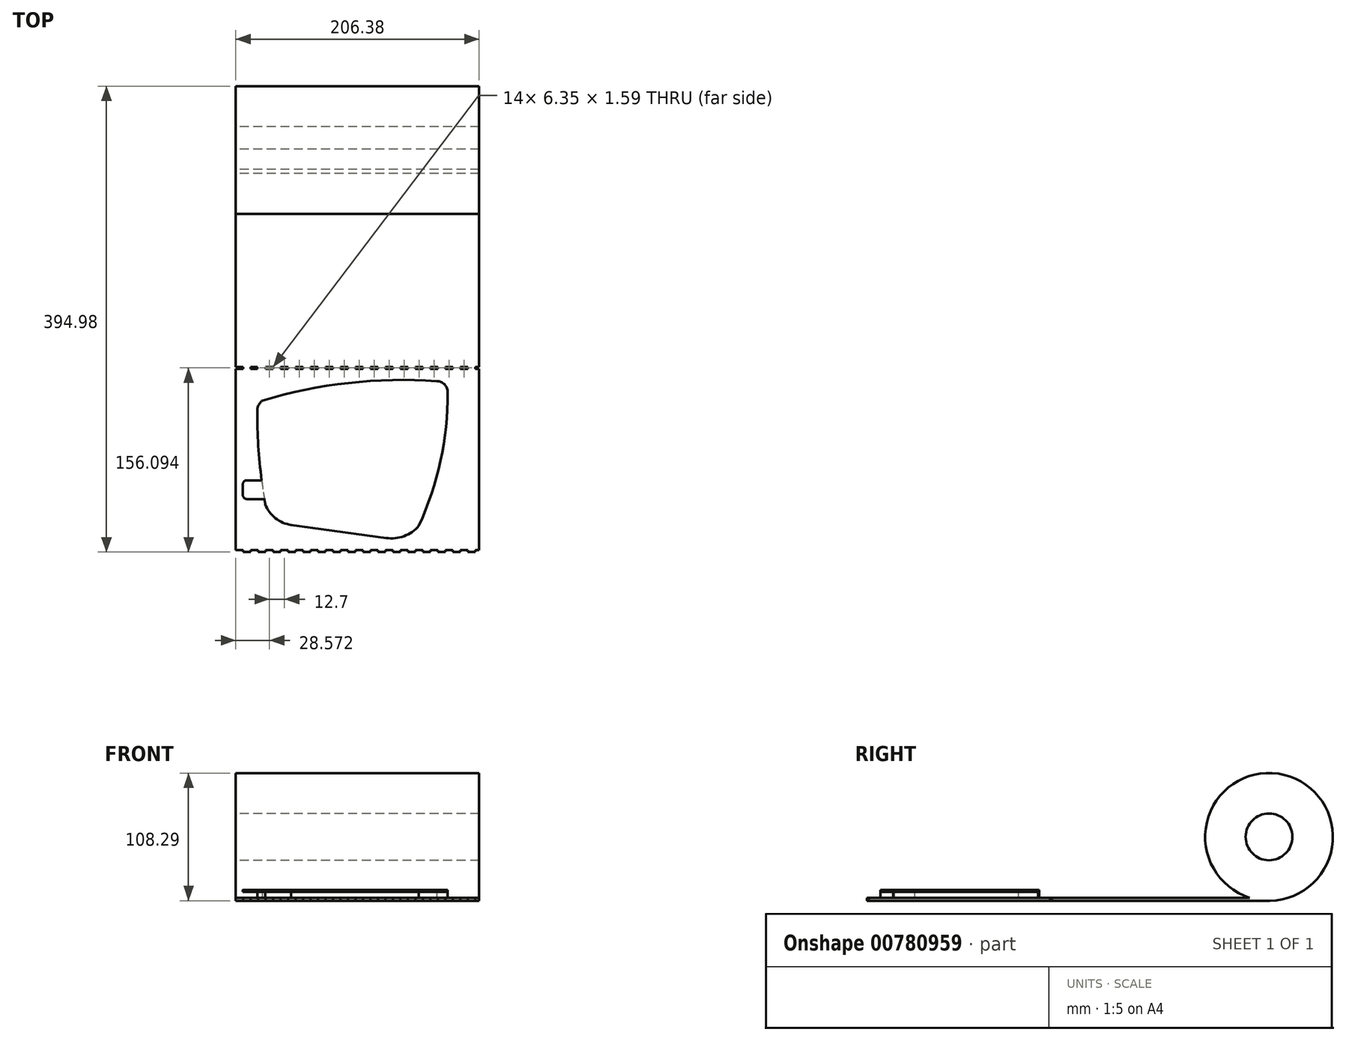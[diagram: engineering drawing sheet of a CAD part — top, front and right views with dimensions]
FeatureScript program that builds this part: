
annotation { "Feature Type Name" : "Feature", "Feature Type Description" : "" }
export const myFeature = defineFeature(function(context is Context, id is Id, definition is map)
    precondition{}
    {
        {
            var Q0;
            Q0=qCreatedBy(makeId("Top.planeOp"),FACE);
            var sketch = newSketch(context, id + "F0", { "sketchPlane" : qUnion([Q0])});
            skArc(sketch, "E0", {"start": v(4.13, 112.63) * mm, "mid": v(1.09, 108.72) * mm, "end": v(0, 103.89) * mm});
            skArc(sketch, "E1", {"start": v(161.62, 119.74) * mm, "mid": v(158.85, 126.48) * mm, "end": v(152.14, 129.33) * mm});
            skArc(sketch, "E2", {"start": v(152.14, 129.33) * mm, "mid": v(77.38, 127.73) * mm, "end": v(4.13, 112.63) * mm});
            skArc(sketch, "E3", {"start": v(137.15, 6.49) * mm, "mid": v(155.43, 61.8) * mm, "end": v(161.62, 119.74) * mm});
            skArc(sketch, "E4", {"start": v(0, 103.89) * mm, "mid": v(1.72, 64.2) * mm, "end": v(6.88, 24.81) * mm});
            skArc(sketch, "E5", {"start": v(6.88, 24.81) * mm, "mid": v(15.4, 12.97) * mm, "end": v(28.88, 7.37) * mm});
            skLineSegment(sketch, "E6", {"start": v(28.88, 7.37) * mm, "end": v(109.24, -3.8) * mm});
            skArc(sketch, "E7", {"start": v(109.24, -3.8) * mm, "mid": v(124.48, -2.16) * mm, "end": v(137.15, 6.49) * mm});
            skSolve(sketch);
        }
        {
            var Q0;
            Q0=makeQuery(id+"F0.imprint","IMPRINT",FACE,{"disambiguationData":[TD([[makeQuery(id+"F0.imprint","IMPRINT",EDGE,{"derivedFrom":sQuery(id+"F0.wireOp",EDGE,"E0")}),1.0]])]});
            var Q1;
            {var subQ0=sQuery(id+"F0.wireOp",EDGE,"PEtAaMhf-ut5D-Udop-JMCo-3PTADJxeKNsQ");Q1=makeQuery(id+"F0.imprint","IMPRINT",FACE,{"disambiguationData":[TD([[makeQuery(id+"F0.imprint","IMPRINT",EDGE,{"derivedFrom":subQ0}),1.0]])]});}
            extrude(context, id + "F1", {"entities" : qUnion([Q0, Q1]), "depth" : 5.08 * mm, "offsetDistance" : 25.4 * mm});
        }
        {
            var Q0;
            Q0=makeQuery(id+"F1.opExtrude","CAP_FACE",FACE,{"disambiguationData":[OSD([sQuery(id+"F0.wireOp",EDGE,"E0"),sQuery(id+"F0.wireOp",EDGE,"E1"),sQuery(id+"F0.wireOp",EDGE,"E2"),sQuery(id+"F0.wireOp",EDGE,"E3"),sQuery(id+"F0.wireOp",EDGE,"E4"),sQuery(id+"F0.wireOp",EDGE,"E5"),sQuery(id+"F0.wireOp",EDGE,"E6"),sQuery(id+"F0.wireOp",EDGE,"E7")])],"isStart":true});
            var sketch = newSketch(context, id + "F2", { "sketchPlane" : qUnion([Q0])});
            skLineSegment(sketch, "E8", {"start": v(188.23, -140.84) * mm, "end": v(-18.15, -140.84) * mm});
            skLineSegment(sketch, "E9", {"start": v(-18.15, -140.84) * mm, "end": v(-18.15, 15.6) * mm});
            skLineSegment(sketch, "E10", {"start": v(-18.15, 15.6) * mm, "end": v(188.23, 15.6) * mm});
            skLineSegment(sketch, "E11", {"start": v(188.23, 15.6) * mm, "end": v(188.23, -140.84) * mm});
            skSolve(sketch);
        }
        {
            var Q0;
            Q0=makeQuery(id+"F2.imprint","IMPRINT",FACE,{"disambiguationData":[TD([[makeQuery(id+"F2.imprint","IMPRINT",EDGE,{"derivedFrom":sQuery(id+"F2.wireOp",EDGE,"E8")}),-1.0]])]});
            var Q1;
            Q1=makeQuery(id+"F2.imprint","IMPRINT",FACE,{"disambiguationData":[TD([[makeQuery(id+"F2.imprint","IMPRINT",EDGE,{"derivedFrom":makeQuery(id+"F1.opExtrude","CAP_EDGE",EDGE,{"disambiguationData":[OSD([sQuery(id+"F0.wireOp",EDGE,"E0")])],"isStart":true})}),-1.0]])]});
            extrude(context, id + "F3", {"entities" : qUnion([Q0, Q1]), "operationType" : NewBodyOperationType.ADD, "depth" : 2.54 * mm, "offsetDistance" : 25.4 * mm});
        }
        {
            var Q0;
            Q0=makeQuery(id+"F3.opExtrude","SWEPT_FACE",FACE,{"disambiguationData":[OSD([sQuery(id+"F2.wireOp",EDGE,"E9")])]});
            var sketch = newSketch(context, id + "F4", { "sketchPlane" : qUnion([Q0])});
            skCircle(sketch, "E12", {"center": v(-325.23, 51.6) * mm, "radius": 19.83 * mm});
            skLineSegment(sketch, "E13", {"start": v(-18.08, 0) * mm, "end": v(-18.08, -2.54) * mm});
            skLineSegment(sketch, "E14", {"start": v(-140.84, -2.54) * mm, "end": v(-326, -2.54) * mm});
            skLineSegment(sketch, "E15", {"start": v(-140.84, 0) * mm, "end": v(-308.82, 0) * mm});
            skPoint(sketch, "E16.second.point", {"position": v(-322.28, 105.67) * mm});
            skArc(sketch, "E17", {"start": v(-308.82, 0) * mm, "mid": v(-333.15, 105.17) * mm, "end": v(-326, -2.54) * mm});
            skSolve(sketch);
        }
        {
            var Q0;
            Q0=makeQuery(id+"F4.imprint","IMPRINT",FACE,{"disambiguationData":[TD([[makeQuery(id+"F4.imprint","IMPRINT",EDGE,{"derivedFrom":sQuery(id+"F4.wireOp",EDGE,"E12")}),-1.0]])]});
            extrude(context, id + "F5", {"entities" : qUnion([Q0]), "operationType" : NewBodyOperationType.ADD, "oppositeDirection" : true, "depth" : 206.38 * mm, "offsetDistance" : 25.4 * mm});
        }
        {
            var Q0;
            Q0=qCreatedBy(makeId("Front.planeOp"),FACE);
            cPlane(context, id + "F6", {"entities" : qUnion([Q0]), "cplaneType" : CPlaneType.OFFSET, "offset" : 139.7 * mm, "oppositeDirection" : true, "width" : 152.4 * mm, "height" : 152.4 * mm});
        }
        {
            var Q0;
            Q0=makeQuery(id+"F3.opExtrude","SWEPT_FACE",FACE,{"disambiguationData":[OSD([sQuery(id+"F2.wireOp",EDGE,"E10")])]});
            var sketch = newSketch(context, id + "F7", { "sketchPlane" : qUnion([Q0])});
            skLineSegment(sketch, "E18", {"start": v(-18.15, -2.54) * mm, "end": v(-18.15, 0) * mm});
            skLineSegment(sketch, "E19", {"start": v(-18.15, 0) * mm, "end": v(-11.8, 0) * mm});
            skLineSegment(sketch, "E20", {"start": v(-11.8, 0) * mm, "end": v(-11.8, -2.54) * mm});
            skLineSegment(sketch, "E21", {"start": v(-11.8, -2.54) * mm, "end": v(-5.45, -2.54) * mm});
            skLineSegment(sketch, "E22", {"start": v(-5.45, -2.54) * mm, "end": v(-5.45, 0) * mm});
            skLineSegment(sketch, "E23", {"start": v(-5.45, 0) * mm, "end": v(0.9, 0) * mm});
            skLineSegment(sketch, "E24", {"start": v(0.9, 0) * mm, "end": v(0.9, -2.54) * mm});
            skLineSegment(sketch, "E25", {"start": v(0.9, -2.54) * mm, "end": v(7.25, -2.54) * mm});
            skLineSegment(sketch, "E26", {"start": v(7.25, -2.54) * mm, "end": v(7.25, 0) * mm});
            skLineSegment(sketch, "E27", {"start": v(7.25, 0) * mm, "end": v(13.6, 0) * mm});
            skLineSegment(sketch, "E28", {"start": v(13.6, 0) * mm, "end": v(13.6, -2.54) * mm});
            skLineSegment(sketch, "E29", {"start": v(13.6, -2.54) * mm, "end": v(19.95, -2.54) * mm});
            skLineSegment(sketch, "E30", {"start": v(19.95, -2.54) * mm, "end": v(19.95, 0) * mm});
            skLineSegment(sketch, "E31", {"start": v(19.95, 0) * mm, "end": v(26.3, 0) * mm});
            skLineSegment(sketch, "E32", {"start": v(26.3, 0) * mm, "end": v(26.3, -2.54) * mm});
            skLineSegment(sketch, "E33", {"start": v(26.3, -2.54) * mm, "end": v(32.65, -2.54) * mm});
            skLineSegment(sketch, "E34", {"start": v(32.65, -2.54) * mm, "end": v(32.65, 0) * mm});
            skLineSegment(sketch, "E35", {"start": v(32.65, 0) * mm, "end": v(39, 0) * mm});
            skLineSegment(sketch, "E36", {"start": v(39, 0) * mm, "end": v(39, -2.54) * mm});
            skLineSegment(sketch, "E37", {"start": v(39, -2.54) * mm, "end": v(45.35, -2.54) * mm});
            skLineSegment(sketch, "E38", {"start": v(45.35, -2.54) * mm, "end": v(45.35, 0) * mm});
            skLineSegment(sketch, "E39", {"start": v(45.35, 0) * mm, "end": v(51.7, 0) * mm});
            skLineSegment(sketch, "E40", {"start": v(51.7, 0) * mm, "end": v(51.7, -2.54) * mm});
            skLineSegment(sketch, "E41", {"start": v(51.7, -2.54) * mm, "end": v(58.05, -2.54) * mm});
            skLineSegment(sketch, "E42", {"start": v(58.05, -2.54) * mm, "end": v(58.05, 0) * mm});
            skLineSegment(sketch, "E43", {"start": v(58.05, 0) * mm, "end": v(64.4, 0) * mm});
            skLineSegment(sketch, "E44", {"start": v(64.4, 0) * mm, "end": v(64.4, -2.54) * mm});
            skLineSegment(sketch, "E45", {"start": v(64.4, -2.54) * mm, "end": v(70.75, -2.54) * mm});
            skLineSegment(sketch, "E46", {"start": v(70.75, -2.54) * mm, "end": v(70.75, 0) * mm});
            skLineSegment(sketch, "E47", {"start": v(70.75, 0) * mm, "end": v(77.1, 0) * mm});
            skLineSegment(sketch, "E48", {"start": v(77.1, 0) * mm, "end": v(77.1, -2.54) * mm});
            skLineSegment(sketch, "E49", {"start": v(77.1, -2.54) * mm, "end": v(83.45, -2.54) * mm});
            skLineSegment(sketch, "E50", {"start": v(83.45, -2.54) * mm, "end": v(83.45, 0) * mm});
            skLineSegment(sketch, "E51", {"start": v(83.45, 0) * mm, "end": v(89.8, 0) * mm});
            skLineSegment(sketch, "E52", {"start": v(89.8, 0) * mm, "end": v(89.8, -2.54) * mm});
            skLineSegment(sketch, "E53", {"start": v(89.8, -2.54) * mm, "end": v(96.15, -2.54) * mm});
            skLineSegment(sketch, "E54", {"start": v(96.15, -2.54) * mm, "end": v(96.15, 0) * mm});
            skLineSegment(sketch, "E55", {"start": v(96.15, 0) * mm, "end": v(102.5, 0) * mm});
            skLineSegment(sketch, "E56", {"start": v(102.5, 0) * mm, "end": v(102.5, -2.54) * mm});
            skLineSegment(sketch, "E57", {"start": v(102.5, -2.54) * mm, "end": v(108.85, -2.54) * mm});
            skLineSegment(sketch, "E58", {"start": v(108.85, -2.54) * mm, "end": v(108.85, 0) * mm});
            skLineSegment(sketch, "E59", {"start": v(108.85, 0) * mm, "end": v(115.2, 0) * mm});
            skLineSegment(sketch, "E60", {"start": v(115.2, 0) * mm, "end": v(115.2, -2.54) * mm});
            skLineSegment(sketch, "E61", {"start": v(115.2, -2.54) * mm, "end": v(121.55, -2.54) * mm});
            skLineSegment(sketch, "E62", {"start": v(121.55, -2.54) * mm, "end": v(121.55, 0) * mm});
            skLineSegment(sketch, "E63", {"start": v(121.55, 0) * mm, "end": v(127.9, 0) * mm});
            skLineSegment(sketch, "E64", {"start": v(127.9, 0) * mm, "end": v(127.9, -2.54) * mm});
            skLineSegment(sketch, "E65", {"start": v(127.9, -2.54) * mm, "end": v(134.25, -2.54) * mm});
            skLineSegment(sketch, "E66", {"start": v(134.25, -2.54) * mm, "end": v(134.25, 0) * mm});
            skLineSegment(sketch, "E67", {"start": v(134.25, 0) * mm, "end": v(140.6, 0) * mm});
            skLineSegment(sketch, "E68", {"start": v(140.6, 0) * mm, "end": v(140.6, -2.54) * mm});
            skLineSegment(sketch, "E69", {"start": v(140.6, -2.54) * mm, "end": v(146.95, -2.54) * mm});
            skLineSegment(sketch, "E70", {"start": v(146.95, -2.54) * mm, "end": v(146.95, 0) * mm});
            skLineSegment(sketch, "E71", {"start": v(146.95, 0) * mm, "end": v(153.3, 0) * mm});
            skLineSegment(sketch, "E72", {"start": v(153.3, 0) * mm, "end": v(153.3, -2.54) * mm});
            skLineSegment(sketch, "E73", {"start": v(153.3, -2.54) * mm, "end": v(159.65, -2.54) * mm});
            skLineSegment(sketch, "E74", {"start": v(159.65, -2.54) * mm, "end": v(159.65, 0) * mm});
            skLineSegment(sketch, "E75", {"start": v(159.65, 0) * mm, "end": v(166, 0) * mm});
            skLineSegment(sketch, "E76", {"start": v(166, 0) * mm, "end": v(166, -2.54) * mm});
            skLineSegment(sketch, "E77", {"start": v(166, -2.54) * mm, "end": v(172.35, -2.54) * mm});
            skLineSegment(sketch, "E78", {"start": v(172.35, -2.54) * mm, "end": v(172.35, 0) * mm});
            skLineSegment(sketch, "E79", {"start": v(172.35, 0) * mm, "end": v(178.7, 0) * mm});
            skLineSegment(sketch, "E80", {"start": v(178.7, 0) * mm, "end": v(178.7, -2.54) * mm});
            skLineSegment(sketch, "E81", {"start": v(178.7, -2.54) * mm, "end": v(185.05, -2.54) * mm});
            skLineSegment(sketch, "E82", {"start": v(185.05, -2.54) * mm, "end": v(185.05, 0) * mm});
            skLineSegment(sketch, "E83", {"start": v(185.05, 0) * mm, "end": v(188.23, 0) * mm});
            skLineSegment(sketch, "E84", {"start": v(188.23, 0) * mm, "end": v(188.23, -2.54) * mm});
            skLineSegment(sketch, "E85", {"start": v(-18.15, -2.54) * mm, "end": v(-11.8, -2.54) * mm});
            skLineSegment(sketch, "E86", {"start": v(-5.45, 0) * mm, "end": v(-11.8, 0) * mm});
            skLineSegment(sketch, "E87", {"start": v(-5.45, -2.54) * mm, "end": v(0.9, -2.54) * mm});
            skLineSegment(sketch, "E88", {"start": v(0.9, 0) * mm, "end": v(7.25, 0) * mm});
            skLineSegment(sketch, "E89", {"start": v(7.25, -2.54) * mm, "end": v(13.6, -2.54) * mm});
            skLineSegment(sketch, "E90", {"start": v(13.6, 0) * mm, "end": v(19.95, 0) * mm});
            skLineSegment(sketch, "E91", {"start": v(19.95, -2.54) * mm, "end": v(26.3, -2.54) * mm});
            skLineSegment(sketch, "E92", {"start": v(26.3, 0) * mm, "end": v(32.65, 0) * mm});
            skLineSegment(sketch, "E93", {"start": v(32.65, -2.54) * mm, "end": v(39, -2.54) * mm});
            skLineSegment(sketch, "E94", {"start": v(39, 0) * mm, "end": v(45.35, 0) * mm});
            skLineSegment(sketch, "E95", {"start": v(45.35, -2.54) * mm, "end": v(51.7, -2.54) * mm});
            skLineSegment(sketch, "E96", {"start": v(51.7, 0) * mm, "end": v(58.05, 0) * mm});
            skLineSegment(sketch, "E97", {"start": v(58.05, -2.54) * mm, "end": v(64.4, -2.54) * mm});
            skLineSegment(sketch, "E98", {"start": v(64.4, 0) * mm, "end": v(70.75, 0) * mm});
            skLineSegment(sketch, "E99", {"start": v(70.75, -2.54) * mm, "end": v(77.1, -2.54) * mm});
            skLineSegment(sketch, "E100", {"start": v(77.1, 0) * mm, "end": v(83.45, 0) * mm});
            skLineSegment(sketch, "E101", {"start": v(83.45, -2.54) * mm, "end": v(89.8, -2.54) * mm});
            skLineSegment(sketch, "E102", {"start": v(89.8, 0) * mm, "end": v(96.15, 0) * mm});
            skLineSegment(sketch, "E103", {"start": v(96.15, -2.54) * mm, "end": v(102.5, -2.54) * mm});
            skLineSegment(sketch, "E104", {"start": v(102.5, 0) * mm, "end": v(108.85, 0) * mm});
            skLineSegment(sketch, "E105", {"start": v(108.85, -2.54) * mm, "end": v(115.2, -2.54) * mm});
            skLineSegment(sketch, "E106", {"start": v(115.2, 0) * mm, "end": v(121.55, 0) * mm});
            skLineSegment(sketch, "E107", {"start": v(121.55, -2.54) * mm, "end": v(127.9, -2.54) * mm});
            skLineSegment(sketch, "E108", {"start": v(134.25, -2.54) * mm, "end": v(140.6, -2.54) * mm});
            skLineSegment(sketch, "E109", {"start": v(140.6, 0) * mm, "end": v(146.95, 0) * mm});
            skLineSegment(sketch, "E110", {"start": v(134.25, 0) * mm, "end": v(127.9, 0) * mm});
            skLineSegment(sketch, "E111", {"start": v(146.95, -2.54) * mm, "end": v(153.3, -2.54) * mm});
            skLineSegment(sketch, "E112", {"start": v(153.3, 0) * mm, "end": v(159.65, 0) * mm});
            skLineSegment(sketch, "E113", {"start": v(159.65, -2.54) * mm, "end": v(166, -2.54) * mm});
            skLineSegment(sketch, "E114", {"start": v(166, 0) * mm, "end": v(172.35, 0) * mm});
            skLineSegment(sketch, "E115", {"start": v(172.35, -2.54) * mm, "end": v(178.7, -2.54) * mm});
            skLineSegment(sketch, "E116", {"start": v(178.7, 0) * mm, "end": v(185.05, 0) * mm});
            skLineSegment(sketch, "E117", {"start": v(185.05, -2.54) * mm, "end": v(188.23, -2.54) * mm});
            skSolve(sketch);
        }
        {
            var Q0;
            Q0=makeQuery(id+"F7.imprint","IMPRINT",FACE,{"disambiguationData":[TD([[makeQuery(id+"F7.imprint","IMPRINT",EDGE,{"derivedFrom":sQuery(id+"F7.wireOp",EDGE,"E18")}),-1.0]])]});
            var Q1;
            Q1=makeQuery(id+"F7.imprint","IMPRINT",FACE,{"disambiguationData":[TD([[makeQuery(id+"F7.imprint","IMPRINT",EDGE,{"derivedFrom":sQuery(id+"F7.wireOp",EDGE,"E22")}),-1.0]])]});
            var Q2;
            Q2=makeQuery(id+"F7.imprint","IMPRINT",FACE,{"disambiguationData":[TD([[makeQuery(id+"F7.imprint","IMPRINT",EDGE,{"derivedFrom":sQuery(id+"F7.wireOp",EDGE,"E26")}),-1.0]])]});
            var Q3;
            Q3=makeQuery(id+"F7.imprint","IMPRINT",FACE,{"disambiguationData":[TD([[makeQuery(id+"F7.imprint","IMPRINT",EDGE,{"derivedFrom":sQuery(id+"F7.wireOp",EDGE,"E30")}),-1.0]])]});
            var Q4;
            Q4=makeQuery(id+"F7.imprint","IMPRINT",FACE,{"disambiguationData":[TD([[makeQuery(id+"F7.imprint","IMPRINT",EDGE,{"derivedFrom":sQuery(id+"F7.wireOp",EDGE,"E34")}),-1.0]])]});
            var Q5;
            Q5=makeQuery(id+"F7.imprint","IMPRINT",FACE,{"disambiguationData":[TD([[makeQuery(id+"F7.imprint","IMPRINT",EDGE,{"derivedFrom":sQuery(id+"F7.wireOp",EDGE,"E38")}),-1.0]])]});
            var Q6;
            Q6=makeQuery(id+"F7.imprint","IMPRINT",FACE,{"disambiguationData":[TD([[makeQuery(id+"F7.imprint","IMPRINT",EDGE,{"derivedFrom":sQuery(id+"F7.wireOp",EDGE,"E42")}),-1.0]])]});
            var Q7;
            Q7=makeQuery(id+"F7.imprint","IMPRINT",FACE,{"disambiguationData":[TD([[makeQuery(id+"F7.imprint","IMPRINT",EDGE,{"derivedFrom":sQuery(id+"F7.wireOp",EDGE,"E46")}),-1.0]])]});
            var Q8;
            Q8=makeQuery(id+"F7.imprint","IMPRINT",FACE,{"disambiguationData":[TD([[makeQuery(id+"F7.imprint","IMPRINT",EDGE,{"derivedFrom":sQuery(id+"F7.wireOp",EDGE,"E50")}),-1.0]])]});
            var Q9;
            Q9=makeQuery(id+"F7.imprint","IMPRINT",FACE,{"disambiguationData":[TD([[makeQuery(id+"F7.imprint","IMPRINT",EDGE,{"derivedFrom":sQuery(id+"F7.wireOp",EDGE,"E54")}),-1.0]])]});
            var Q10;
            Q10=makeQuery(id+"F7.imprint","IMPRINT",FACE,{"disambiguationData":[TD([[makeQuery(id+"F7.imprint","IMPRINT",EDGE,{"derivedFrom":sQuery(id+"F7.wireOp",EDGE,"E58")}),-1.0]])]});
            var Q11;
            Q11=makeQuery(id+"F7.imprint","IMPRINT",FACE,{"disambiguationData":[TD([[makeQuery(id+"F7.imprint","IMPRINT",EDGE,{"derivedFrom":sQuery(id+"F7.wireOp",EDGE,"E62")}),-1.0]])]});
            var Q12;
            Q12=makeQuery(id+"F7.imprint","IMPRINT",FACE,{"disambiguationData":[TD([[makeQuery(id+"F7.imprint","IMPRINT",EDGE,{"derivedFrom":sQuery(id+"F7.wireOp",EDGE,"E66")}),-1.0]])]});
            var Q13;
            Q13=makeQuery(id+"F7.imprint","IMPRINT",FACE,{"disambiguationData":[TD([[makeQuery(id+"F7.imprint","IMPRINT",EDGE,{"derivedFrom":sQuery(id+"F7.wireOp",EDGE,"E70")}),-1.0]])]});
            var Q14;
            Q14=makeQuery(id+"F7.imprint","IMPRINT",FACE,{"disambiguationData":[TD([[makeQuery(id+"F7.imprint","IMPRINT",EDGE,{"derivedFrom":sQuery(id+"F7.wireOp",EDGE,"E74")}),-1.0]])]});
            var Q15;
            Q15=makeQuery(id+"F7.imprint","IMPRINT",FACE,{"disambiguationData":[TD([[makeQuery(id+"F7.imprint","IMPRINT",EDGE,{"derivedFrom":sQuery(id+"F7.wireOp",EDGE,"E78")}),-1.0]])]});
            var Q16;
            Q16=makeQuery(id+"F7.imprint","IMPRINT",FACE,{"disambiguationData":[TD([[makeQuery(id+"F7.imprint","IMPRINT",EDGE,{"derivedFrom":sQuery(id+"F7.wireOp",EDGE,"E82")}),-1.0]])]});
            extrude(context, id + "F8", {"entities" : qUnion([Q0, Q1, Q2, Q3, Q4, Q5, Q6, Q7, Q8, Q9, Q10, Q11, Q12, Q13, Q14, Q15, Q16]), "operationType" : NewBodyOperationType.REMOVE, "oppositeDirection" : true, "depth" : 1.59 * mm, "offsetDistance" : 25.4 * mm});
        }
        {
            var Q0;
            Q0=qCreatedBy(id+"F6.planeOp",FACE);
            var sketch = newSketch(context, id + "F9", { "sketchPlane" : qUnion([Q0])});
            skLineSegment(sketch, "E118", {"start": v(0, 0) * mm, "end": v(0, -2.54) * mm});
            skLineSegment(sketch, "E119", {"start": v(-18.15, 0) * mm, "end": v(-18.15, -2.54) * mm});
            skLineSegment(sketch, "E120.bottom", {"start": v(-18.15, 0) * mm, "end": v(-11.8, 0) * mm});
            skLineSegment(sketch, "E120.top", {"start": v(-18.15, -2.54) * mm, "end": v(-11.8, -2.54) * mm});
            skLineSegment(sketch, "E120.right", {"start": v(-11.8, 0) * mm, "end": v(-11.8, -2.54) * mm});
            skLineSegment(sketch, "E121.bottom", {"start": v(-11.8, 0) * mm, "end": v(-5.45, 0) * mm});
            skLineSegment(sketch, "E121.top", {"start": v(-11.8, -2.54) * mm, "end": v(-5.45, -2.54) * mm});
            skLineSegment(sketch, "E121.right", {"start": v(-5.45, 0) * mm, "end": v(-5.45, -2.54) * mm});
            skLineSegment(sketch, "E122.bottom", {"start": v(-5.45, 0) * mm, "end": v(0.9, 0) * mm});
            skLineSegment(sketch, "E122.top", {"start": v(-5.45, -2.54) * mm, "end": v(0.9, -2.54) * mm});
            skLineSegment(sketch, "E122.right", {"start": v(0.9, 0) * mm, "end": v(0.9, -2.54) * mm});
            skLineSegment(sketch, "E123.bottom", {"start": v(0.9, 0) * mm, "end": v(7.25, 0) * mm});
            skLineSegment(sketch, "E123.top", {"start": v(0.9, -2.54) * mm, "end": v(7.25, -2.54) * mm});
            skLineSegment(sketch, "E123.right", {"start": v(7.25, 0) * mm, "end": v(7.25, -2.54) * mm});
            skLineSegment(sketch, "E124.bottom", {"start": v(7.25, 0) * mm, "end": v(13.6, 0) * mm});
            skLineSegment(sketch, "E124.top", {"start": v(7.25, -2.54) * mm, "end": v(13.6, -2.54) * mm});
            skLineSegment(sketch, "E124.right", {"start": v(13.6, 0) * mm, "end": v(13.6, -2.54) * mm});
            skLineSegment(sketch, "E125.bottom", {"start": v(13.6, 0) * mm, "end": v(19.95, 0) * mm});
            skLineSegment(sketch, "E125.top", {"start": v(13.6, -2.54) * mm, "end": v(19.95, -2.54) * mm});
            skLineSegment(sketch, "E125.right", {"start": v(19.95, 0) * mm, "end": v(19.95, -2.54) * mm});
            skLineSegment(sketch, "E126.bottom", {"start": v(19.95, 0) * mm, "end": v(26.3, 0) * mm});
            skLineSegment(sketch, "E126.top", {"start": v(19.95, -2.54) * mm, "end": v(26.3, -2.54) * mm});
            skLineSegment(sketch, "E126.right", {"start": v(26.3, 0) * mm, "end": v(26.3, -2.54) * mm});
            skLineSegment(sketch, "E127.bottom", {"start": v(26.3, 0) * mm, "end": v(32.65, 0) * mm});
            skLineSegment(sketch, "E127.top", {"start": v(26.3, -2.54) * mm, "end": v(32.65, -2.54) * mm});
            skLineSegment(sketch, "E127.right", {"start": v(32.65, 0) * mm, "end": v(32.65, -2.54) * mm});
            skLineSegment(sketch, "E128.bottom", {"start": v(32.65, 0) * mm, "end": v(39, 0) * mm});
            skLineSegment(sketch, "E128.top", {"start": v(32.65, -2.54) * mm, "end": v(39, -2.54) * mm});
            skLineSegment(sketch, "E128.right", {"start": v(39, 0) * mm, "end": v(39, -2.54) * mm});
            skLineSegment(sketch, "E129.bottom", {"start": v(39, 0) * mm, "end": v(45.35, 0) * mm});
            skLineSegment(sketch, "E129.top", {"start": v(39, -2.54) * mm, "end": v(45.35, -2.54) * mm});
            skLineSegment(sketch, "E129.right", {"start": v(45.35, 0) * mm, "end": v(45.35, -2.54) * mm});
            skLineSegment(sketch, "E130.bottom", {"start": v(45.35, 0) * mm, "end": v(51.7, 0) * mm});
            skLineSegment(sketch, "E130.top", {"start": v(45.35, -2.54) * mm, "end": v(51.7, -2.54) * mm});
            skLineSegment(sketch, "E130.right", {"start": v(51.7, 0) * mm, "end": v(51.7, -2.54) * mm});
            skLineSegment(sketch, "E131.bottom", {"start": v(51.7, 0) * mm, "end": v(58.05, 0) * mm});
            skLineSegment(sketch, "E131.top", {"start": v(51.7, -2.54) * mm, "end": v(58.05, -2.54) * mm});
            skLineSegment(sketch, "E131.right", {"start": v(58.05, 0) * mm, "end": v(58.05, -2.54) * mm});
            skLineSegment(sketch, "E132.bottom", {"start": v(58.05, 0) * mm, "end": v(64.4, 0) * mm});
            skLineSegment(sketch, "E132.top", {"start": v(58.05, -2.54) * mm, "end": v(64.4, -2.54) * mm});
            skLineSegment(sketch, "E132.right", {"start": v(64.4, 0) * mm, "end": v(64.4, -2.54) * mm});
            skLineSegment(sketch, "E133.bottom", {"start": v(64.4, 0) * mm, "end": v(70.75, 0) * mm});
            skLineSegment(sketch, "E133.top", {"start": v(64.4, -2.54) * mm, "end": v(70.75, -2.54) * mm});
            skLineSegment(sketch, "E133.right", {"start": v(70.75, 0) * mm, "end": v(70.75, -2.54) * mm});
            skLineSegment(sketch, "E134.bottom", {"start": v(70.75, 0) * mm, "end": v(77.1, 0) * mm});
            skLineSegment(sketch, "E134.top", {"start": v(70.75, -2.54) * mm, "end": v(77.1, -2.54) * mm});
            skLineSegment(sketch, "E134.right", {"start": v(77.1, 0) * mm, "end": v(77.1, -2.54) * mm});
            skLineSegment(sketch, "E135.bottom", {"start": v(77.1, 0) * mm, "end": v(83.45, 0) * mm});
            skLineSegment(sketch, "E135.top", {"start": v(77.1, -2.54) * mm, "end": v(83.45, -2.54) * mm});
            skLineSegment(sketch, "E135.right", {"start": v(83.45, 0) * mm, "end": v(83.45, -2.54) * mm});
            skLineSegment(sketch, "E136.bottom", {"start": v(83.45, 0) * mm, "end": v(89.8, 0) * mm});
            skLineSegment(sketch, "E136.top", {"start": v(83.45, -2.54) * mm, "end": v(89.8, -2.54) * mm});
            skLineSegment(sketch, "E136.right", {"start": v(89.8, 0) * mm, "end": v(89.8, -2.54) * mm});
            skLineSegment(sketch, "E137.bottom", {"start": v(89.8, 0) * mm, "end": v(96.15, 0) * mm});
            skLineSegment(sketch, "E137.top", {"start": v(89.8, -2.54) * mm, "end": v(96.15, -2.54) * mm});
            skLineSegment(sketch, "E137.right", {"start": v(96.15, 0) * mm, "end": v(96.15, -2.54) * mm});
            skLineSegment(sketch, "E138.bottom", {"start": v(96.15, 0) * mm, "end": v(102.5, 0) * mm});
            skLineSegment(sketch, "E138.top", {"start": v(96.15, -2.54) * mm, "end": v(102.5, -2.54) * mm});
            skLineSegment(sketch, "E138.right", {"start": v(102.5, 0) * mm, "end": v(102.5, -2.54) * mm});
            skLineSegment(sketch, "E139.bottom", {"start": v(102.5, 0) * mm, "end": v(108.85, 0) * mm});
            skLineSegment(sketch, "E139.top", {"start": v(102.5, -2.54) * mm, "end": v(108.85, -2.54) * mm});
            skLineSegment(sketch, "E139.right", {"start": v(108.85, 0) * mm, "end": v(108.85, -2.54) * mm});
            skLineSegment(sketch, "E140.bottom", {"start": v(108.85, 0) * mm, "end": v(115.2, 0) * mm});
            skLineSegment(sketch, "E140.top", {"start": v(108.85, -2.54) * mm, "end": v(115.2, -2.54) * mm});
            skLineSegment(sketch, "E140.right", {"start": v(115.2, 0) * mm, "end": v(115.2, -2.54) * mm});
            skLineSegment(sketch, "E141.bottom", {"start": v(115.2, 0) * mm, "end": v(121.55, 0) * mm});
            skLineSegment(sketch, "E141.top", {"start": v(115.2, -2.54) * mm, "end": v(121.55, -2.54) * mm});
            skLineSegment(sketch, "E141.right", {"start": v(121.55, 0) * mm, "end": v(121.55, -2.54) * mm});
            skLineSegment(sketch, "E142.bottom", {"start": v(121.55, 0) * mm, "end": v(127.9, 0) * mm});
            skLineSegment(sketch, "E142.top", {"start": v(121.55, -2.54) * mm, "end": v(127.9, -2.54) * mm});
            skLineSegment(sketch, "E142.right", {"start": v(127.9, 0) * mm, "end": v(127.9, -2.54) * mm});
            skLineSegment(sketch, "E143.bottom", {"start": v(127.9, 0) * mm, "end": v(134.25, 0) * mm});
            skLineSegment(sketch, "E143.top", {"start": v(127.9, -2.54) * mm, "end": v(134.25, -2.54) * mm});
            skLineSegment(sketch, "E143.right", {"start": v(134.25, 0) * mm, "end": v(134.25, -2.54) * mm});
            skLineSegment(sketch, "E144.bottom", {"start": v(134.25, -2.54) * mm, "end": v(140.6, -2.54) * mm});
            skLineSegment(sketch, "E144.top", {"start": v(134.25, 0) * mm, "end": v(140.6, 0) * mm});
            skLineSegment(sketch, "E144.left", {"start": v(134.25, -2.54) * mm, "end": v(134.25, 0) * mm});
            skLineSegment(sketch, "E144.right", {"start": v(140.6, -2.54) * mm, "end": v(140.6, 0) * mm});
            skLineSegment(sketch, "E145.bottom", {"start": v(140.6, 0) * mm, "end": v(146.95, 0) * mm});
            skLineSegment(sketch, "E145.top", {"start": v(140.6, -2.54) * mm, "end": v(146.95, -2.54) * mm});
            skLineSegment(sketch, "E145.left", {"start": v(140.6, 0) * mm, "end": v(140.6, -2.54) * mm});
            skLineSegment(sketch, "E145.right", {"start": v(146.95, 0) * mm, "end": v(146.95, -2.54) * mm});
            skLineSegment(sketch, "E146.bottom", {"start": v(146.95, 0) * mm, "end": v(153.3, 0) * mm});
            skLineSegment(sketch, "E146.top", {"start": v(146.95, -2.54) * mm, "end": v(153.3, -2.54) * mm});
            skLineSegment(sketch, "E146.right", {"start": v(153.3, 0) * mm, "end": v(153.3, -2.54) * mm});
            skLineSegment(sketch, "E147.bottom", {"start": v(153.3, 0) * mm, "end": v(159.65, 0) * mm});
            skLineSegment(sketch, "E147.top", {"start": v(153.3, -2.54) * mm, "end": v(159.65, -2.54) * mm});
            skLineSegment(sketch, "E147.right", {"start": v(159.65, 0) * mm, "end": v(159.65, -2.54) * mm});
            skLineSegment(sketch, "E148.bottom", {"start": v(159.65, 0) * mm, "end": v(166, 0) * mm});
            skLineSegment(sketch, "E148.top", {"start": v(159.65, -2.54) * mm, "end": v(166, -2.54) * mm});
            skLineSegment(sketch, "E148.right", {"start": v(166, 0) * mm, "end": v(166, -2.54) * mm});
            skLineSegment(sketch, "E149.bottom", {"start": v(166, 0) * mm, "end": v(172.35, 0) * mm});
            skLineSegment(sketch, "E149.top", {"start": v(166, -2.54) * mm, "end": v(172.35, -2.54) * mm});
            skLineSegment(sketch, "E149.right", {"start": v(172.35, 0) * mm, "end": v(172.35, -2.54) * mm});
            skLineSegment(sketch, "E150.bottom", {"start": v(172.35, 0) * mm, "end": v(178.7, 0) * mm});
            skLineSegment(sketch, "E150.top", {"start": v(172.35, -2.54) * mm, "end": v(178.7, -2.54) * mm});
            skLineSegment(sketch, "E150.right", {"start": v(178.7, 0) * mm, "end": v(178.7, -2.54) * mm});
            skLineSegment(sketch, "E151.bottom", {"start": v(178.7, 0) * mm, "end": v(185.05, 0) * mm});
            skLineSegment(sketch, "E151.top", {"start": v(178.7, -2.54) * mm, "end": v(185.05, -2.54) * mm});
            skLineSegment(sketch, "E151.right", {"start": v(185.05, 0) * mm, "end": v(185.05, -2.54) * mm});
            skLineSegment(sketch, "E152.bottom", {"start": v(185.05, 0) * mm, "end": v(189.75, 0) * mm});
            skLineSegment(sketch, "E152.top", {"start": v(185.05, -2.54) * mm, "end": v(189.75, -2.54) * mm});
            skLineSegment(sketch, "E152.right", {"start": v(189.75, 0) * mm, "end": v(189.75, -2.54) * mm});
            skSolve(sketch);
        }
        {
            var Q0;
            Q0=makeQuery(id+"F9.imprint","IMPRINT",FACE,{"disambiguationData":[TD([[makeQuery(id+"F9.imprint","IMPRINT",EDGE,{"derivedFrom":sQuery(id+"F9.wireOp",EDGE,"E119")}),1.0]])]});
            var Q1;
            {var subQ0=sQuery(id+"F9.wireOp",EDGE,"E118");Q1=makeQuery(id+"F9.imprint","IMPRINT",FACE,{"disambiguationData":[TD([[makeQuery(id+"F9.imprint","IMPRINT",EDGE,{"derivedFrom":subQ0}),-1.0]])]});}
            var Q2;
            Q2=makeQuery(id+"F9.imprint","IMPRINT",FACE,{"disambiguationData":[TD([[makeQuery(id+"F9.imprint","IMPRINT",EDGE,{"derivedFrom":sQuery(id+"F9.wireOp",EDGE,"E124.bottom")}),-1.0]])]});
            var Q3;
            Q3=makeQuery(id+"F9.imprint","IMPRINT",FACE,{"disambiguationData":[TD([[makeQuery(id+"F9.imprint","IMPRINT",EDGE,{"derivedFrom":sQuery(id+"F9.wireOp",EDGE,"E126.bottom")}),-1.0]])]});
            var Q4;
            Q4=makeQuery(id+"F9.imprint","IMPRINT",FACE,{"disambiguationData":[TD([[makeQuery(id+"F9.imprint","IMPRINT",EDGE,{"derivedFrom":sQuery(id+"F9.wireOp",EDGE,"E128.bottom")}),-1.0]])]});
            var Q5;
            Q5=makeQuery(id+"F9.imprint","IMPRINT",FACE,{"disambiguationData":[TD([[makeQuery(id+"F9.imprint","IMPRINT",EDGE,{"derivedFrom":sQuery(id+"F9.wireOp",EDGE,"E152.bottom")}),-1.0]])]});
            var Q6;
            Q6=makeQuery(id+"F9.imprint","IMPRINT",FACE,{"disambiguationData":[TD([[makeQuery(id+"F9.imprint","IMPRINT",EDGE,{"derivedFrom":sQuery(id+"F9.wireOp",EDGE,"E130.bottom")}),-1.0]])]});
            var Q7;
            Q7=makeQuery(id+"F9.imprint","IMPRINT",FACE,{"disambiguationData":[TD([[makeQuery(id+"F9.imprint","IMPRINT",EDGE,{"derivedFrom":sQuery(id+"F9.wireOp",EDGE,"E132.bottom")}),-1.0]])]});
            var Q8;
            Q8=makeQuery(id+"F9.imprint","IMPRINT",FACE,{"disambiguationData":[TD([[makeQuery(id+"F9.imprint","IMPRINT",EDGE,{"derivedFrom":sQuery(id+"F9.wireOp",EDGE,"E134.bottom")}),-1.0]])]});
            var Q9;
            Q9=makeQuery(id+"F9.imprint","IMPRINT",FACE,{"disambiguationData":[TD([[makeQuery(id+"F9.imprint","IMPRINT",EDGE,{"derivedFrom":sQuery(id+"F9.wireOp",EDGE,"E136.bottom")}),-1.0]])]});
            var Q10;
            Q10=makeQuery(id+"F9.imprint","IMPRINT",FACE,{"disambiguationData":[TD([[makeQuery(id+"F9.imprint","IMPRINT",EDGE,{"derivedFrom":sQuery(id+"F9.wireOp",EDGE,"E138.bottom")}),-1.0]])]});
            var Q11;
            Q11=makeQuery(id+"F9.imprint","IMPRINT",FACE,{"disambiguationData":[TD([[makeQuery(id+"F9.imprint","IMPRINT",EDGE,{"derivedFrom":sQuery(id+"F9.wireOp",EDGE,"E140.bottom")}),-1.0]])]});
            var Q12;
            Q12=makeQuery(id+"F9.imprint","IMPRINT",FACE,{"disambiguationData":[TD([[makeQuery(id+"F9.imprint","IMPRINT",EDGE,{"derivedFrom":sQuery(id+"F9.wireOp",EDGE,"E142.bottom")}),-1.0]])]});
            var Q13;
            Q13=makeQuery(id+"F9.imprint","IMPRINT",FACE,{"disambiguationData":[TD([[makeQuery(id+"F9.imprint","IMPRINT",EDGE,{"derivedFrom":sQuery(id+"F9.wireOp",EDGE,"E144.bottom")}),1.0]])]});
            var Q14;
            Q14=makeQuery(id+"F9.imprint","IMPRINT",FACE,{"disambiguationData":[TD([[makeQuery(id+"F9.imprint","IMPRINT",EDGE,{"derivedFrom":sQuery(id+"F9.wireOp",EDGE,"E146.bottom")}),-1.0]])]});
            var Q15;
            Q15=makeQuery(id+"F9.imprint","IMPRINT",FACE,{"disambiguationData":[TD([[makeQuery(id+"F9.imprint","IMPRINT",EDGE,{"derivedFrom":sQuery(id+"F9.wireOp",EDGE,"E148.bottom")}),-1.0]])]});
            var Q16;
            Q16=makeQuery(id+"F9.imprint","IMPRINT",FACE,{"disambiguationData":[TD([[makeQuery(id+"F9.imprint","IMPRINT",EDGE,{"derivedFrom":sQuery(id+"F9.wireOp",EDGE,"E150.bottom")}),-1.0]])]});
            extrude(context, id + "F10", {"entities" : qUnion([Q0, Q1, Q2, Q3, Q4, Q5, Q6, Q7, Q8, Q9, Q10, Q11, Q12, Q13, Q14, Q15, Q16]), "operationType" : NewBodyOperationType.REMOVE, "oppositeDirection" : true, "depth" : 1.59 * mm, "offsetDistance" : 25.4 * mm});
        }
        {
            var Q0;
            Q0=makeQuery(id+"F1.opExtrude","CAP_FACE",FACE,{"disambiguationData":[OSD([sQuery(id+"F0.wireOp",EDGE,"E0"),sQuery(id+"F0.wireOp",EDGE,"E1"),sQuery(id+"F0.wireOp",EDGE,"E2"),sQuery(id+"F0.wireOp",EDGE,"E3"),sQuery(id+"F0.wireOp",EDGE,"E4"),sQuery(id+"F0.wireOp",EDGE,"E5"),sQuery(id+"F0.wireOp",EDGE,"E6"),sQuery(id+"F0.wireOp",EDGE,"E7")])],"isStart":false});
            var sketch = newSketch(context, id + "F11", { "sketchPlane" : qUnion([Q0])});
            skLineSegment(sketch, "E153", {"start": v(3.78, 45.2) * mm, "end": v(-8.92, 45.2) * mm});
            skLineSegment(sketch, "E154", {"start": v(-12.1, 42.02) * mm, "end": v(-12.1, 32.5) * mm});
            skLineSegment(sketch, "E155", {"start": v(-8.92, 29.32) * mm, "end": v(6.12, 29.32) * mm});
            skPoint(sketch, "E156.visualSharp", {"position": v(-12.1, 45.2) * mm});
            skArc(sketch, "E156.filletArc", {"start": v(-8.92, 45.2) * mm, "mid": v(-11.17, 44.27) * mm, "end": v(-12.1, 42.02) * mm});
            skPoint(sketch, "E157.visualSharp", {"position": v(-12.1, 29.32) * mm});
            skArc(sketch, "E157.filletArc", {"start": v(-12.1, 32.5) * mm, "mid": v(-11.17, 30.25) * mm, "end": v(-8.92, 29.32) * mm});
            skSolve(sketch);
        }
        {
            var Q0;
            {var subQ0=makeQuery(id+"F1.opExtrude","CAP_EDGE",EDGE,{"disambiguationData":[OSD([sQuery(id+"F0.wireOp",EDGE,"E0")])],"isStart":false});Q0=makeQuery(id+"F11.imprint","IMPRINT",FACE,{"disambiguationData":[TD([[makeQuery(id+"F11.imprint","IMPRINT",EDGE,{"derivedFrom":subQ0}),1.0]])]});}
            var Q1;
            {var subQ0=sQuery(id+"F11.wireOp",EDGE,"aQNFZi3p-mO67-hDzx-iR2I-60T21Jgk8zFz");Q1=makeQuery(id+"F11.imprint","IMPRINT",FACE,{"disambiguationData":[TD([[makeQuery(id+"F11.imprint","IMPRINT",EDGE,{"derivedFrom":subQ0}),1.0]])]});}
            var Q2;
            {var subQ0=sQuery(id+"F11.wireOp",EDGE,"E153");Q2=makeQuery(id+"F11.imprint","IMPRINT",FACE,{"disambiguationData":[TD([[makeQuery(id+"F11.imprint","IMPRINT",EDGE,{"derivedFrom":subQ0}),1.0]])]});}
            extrude(context, id + "F12", {"entities" : qUnion([Q0, Q1, Q2]), "depth" : 1.59 * mm, "offsetDistance" : 25.4 * mm});
        }
    });
